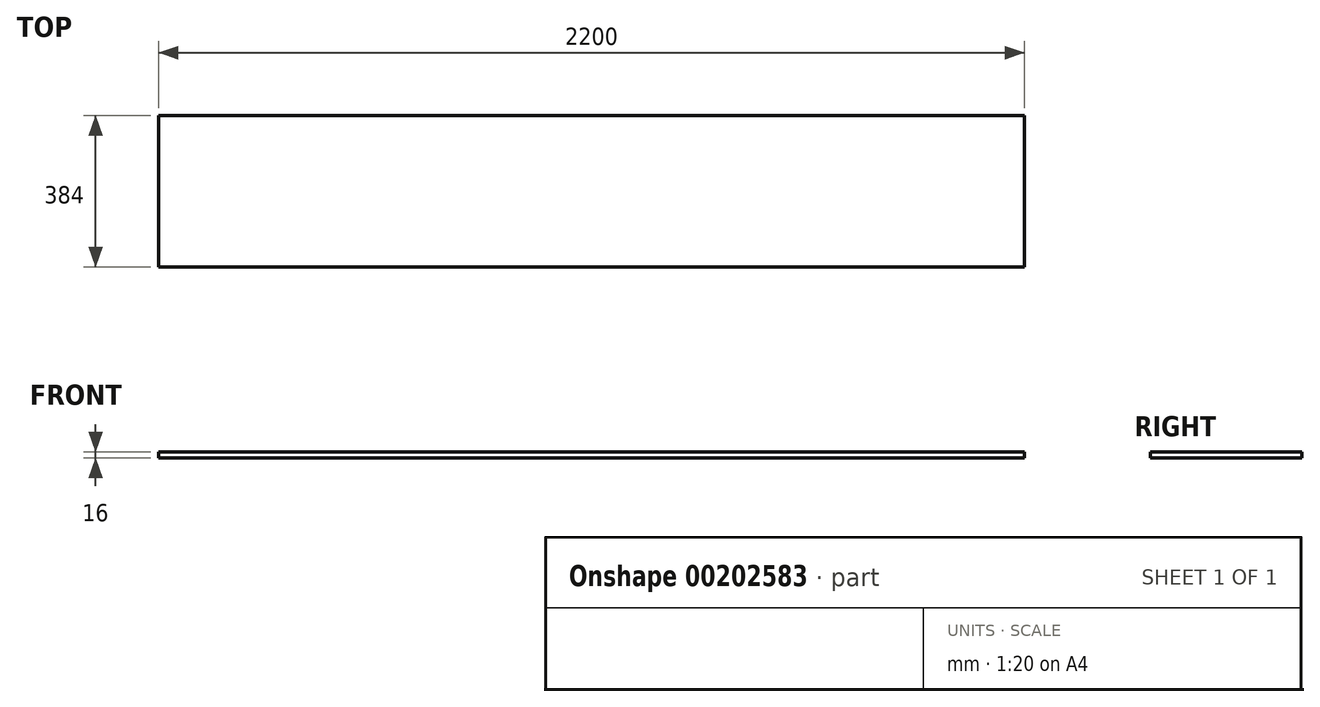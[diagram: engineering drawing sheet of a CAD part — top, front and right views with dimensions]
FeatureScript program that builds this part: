
annotation { "Feature Type Name" : "Feature", "Feature Type Description" : "" }
export const myFeature = defineFeature(function(context is Context, id is Id, definition is map)
    precondition{}
    {
        {
            var Q0;
            Q0=qCreatedBy(makeId("Top.planeOp"),FACE);
            var sketch = newSketch(context, id + "F0", { "sketchPlane" : qUnion([Q0])});
            skLineSegment(sketch, "E0.bottom", {"start": v(-864.34, -235.28) * mm, "end": v(1335.66, -235.28) * mm});
            skLineSegment(sketch, "E0.top", {"start": v(-864.34, 148.72) * mm, "end": v(1335.66, 148.72) * mm});
            skLineSegment(sketch, "E0.left", {"start": v(-864.34, -235.28) * mm, "end": v(-864.34, 148.72) * mm});
            skLineSegment(sketch, "E0.right", {"start": v(1335.66, -235.28) * mm, "end": v(1335.66, 148.72) * mm});
            skSolve(sketch);
        }
        {
            var Q0;
            Q0=makeQuery(id+"F0.imprint","IMPRINT",FACE,{"disambiguationData":[TD([[makeQuery(id+"F0.imprint","IMPRINT",EDGE,{"derivedFrom":sQuery(id+"F0.wireOp",EDGE,"E0.bottom")}),1.0]])]});
            extrude(context, id + "F1", {"entities" : qUnion([Q0]), "depth" : 16 * mm});
        }
    });
